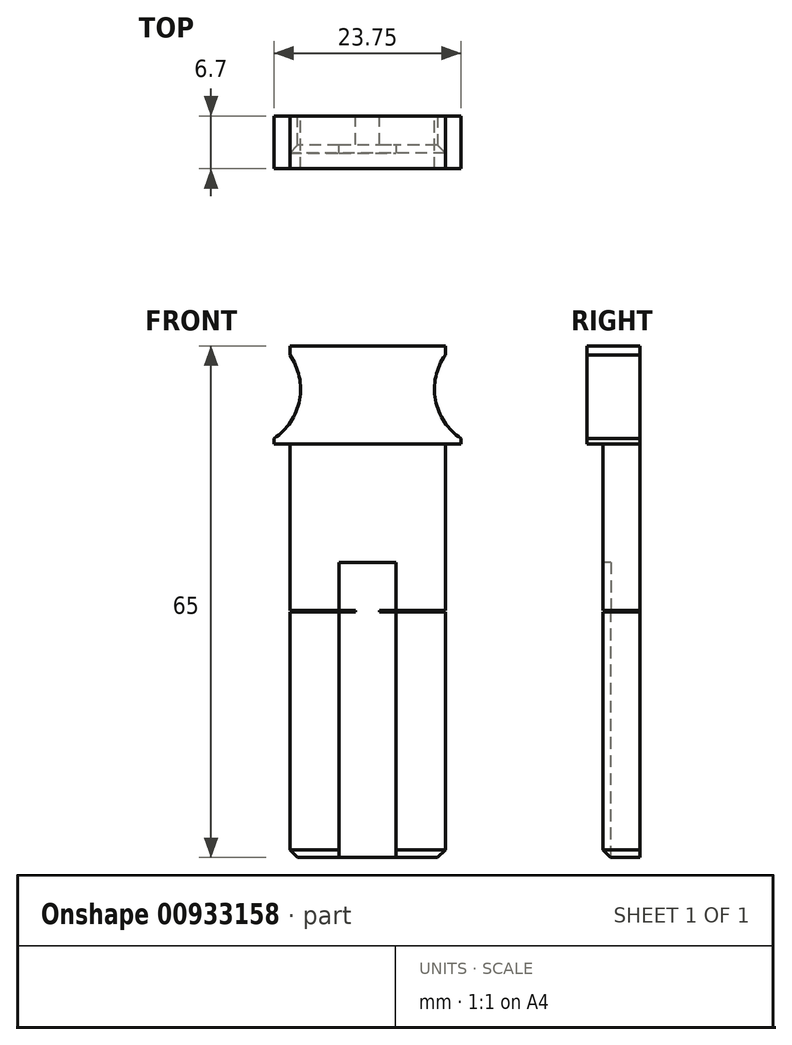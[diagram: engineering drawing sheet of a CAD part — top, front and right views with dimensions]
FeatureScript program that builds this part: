
annotation { "Feature Type Name" : "Feature", "Feature Type Description" : "" }
export const myFeature = defineFeature(function(context is Context, id is Id, definition is map)
    precondition{}
    {
        {
            var Q0;
            Q0=qCreatedBy(makeId("Front.planeOp"),FACE);
            var sketch = newSketch(context, id + "F0", { "sketchPlane" : qUnion([Q0])});
            skLineSegment(sketch, "E0.bottom", {"start": v(0, 0) * mm, "end": v(19.75, 0) * mm});
            skLineSegment(sketch, "E0.top", {"start": v(0, 65) * mm, "end": v(19.75, 65) * mm});
            skLineSegment(sketch, "E0.left", {"start": v(0, 0) * mm, "end": v(0, 65) * mm});
            skLineSegment(sketch, "E0.right", {"start": v(19.75, 0) * mm, "end": v(19.75, 65) * mm});
            skLineSegment(sketch, "E1", {"start": v(9.87, 65) * mm, "end": v(9.87, 0) * mm, "construction": true});
            skPoint(sketch, "E2", {"position": v(9.87, 38.5) * mm});
            skLineSegment(sketch, "E3", {"start": v(-8.82, 31.3) * mm, "end": v(33.74, 31.3) * mm, "construction": true});
            skLineSegment(sketch, "E4", {"start": v(0, 31.2) * mm, "end": v(0, 31.4) * mm});
            skCircle(sketch, "E5", {"center": v(25.88, 59.5) * mm, "radius": 7.5 * mm});
            skCircle(sketch, "E6.MirrorC", {"center": v(-6.13, 59.5) * mm, "radius": 7.5 * mm});
            skLineSegment(sketch, "E7.bottom", {"start": v(0, 31.4) * mm, "end": v(8.32, 31.4) * mm});
            skLineSegment(sketch, "E7.top", {"start": v(0, 31.4) * mm, "end": v(8.32, 31.4) * mm});
            skLineSegment(sketch, "E7.left", {"start": v(0, 31.4) * mm, "end": v(0, 31.4) * mm});
            skLineSegment(sketch, "E7.right", {"start": v(8.32, 31.4) * mm, "end": v(8.32, 31.4) * mm});
            skLineSegment(sketch, "E8", {"start": v(8.32, 31.4) * mm, "end": v(8.32, 31.2) * mm});
            skLineSegment(sketch, "E9", {"start": v(8.32, 31.2) * mm, "end": v(0, 31.2) * mm});
            skLineSegment(sketch, "E10", {"start": v(0, 31.4) * mm, "end": v(0, 31.2) * mm});
            skLineSegment(sketch, "E11.MirrorCS", {"start": v(19.75, 31.4) * mm, "end": v(11.43, 31.4) * mm});
            skLineSegment(sketch, "E12.MirrorCS", {"start": v(11.42, 31.4) * mm, "end": v(11.42, 31.2) * mm});
            skLineSegment(sketch, "E13.MirrorCS", {"start": v(11.43, 31.2) * mm, "end": v(19.75, 31.2) * mm});
            skLineSegment(sketch, "E14.MirrorCS", {"start": v(19.75, 31.4) * mm, "end": v(19.75, 31.2) * mm});
            skLineSegment(sketch, "E15.bottom", {"start": v(0, 52.5) * mm, "end": v(-2, 52.5) * mm});
            skLineSegment(sketch, "E15.top", {"start": v(0, 65.03) * mm, "end": v(-2, 65.03) * mm});
            skLineSegment(sketch, "E15.left", {"start": v(0, 52.5) * mm, "end": v(0, 65.03) * mm});
            skLineSegment(sketch, "E15.right", {"start": v(-2, 52.5) * mm, "end": v(-2, 65.03) * mm});
            skLineSegment(sketch, "E16.MirrorCS", {"start": v(19.75, 65.03) * mm, "end": v(21.75, 65.03) * mm});
            skLineSegment(sketch, "E17.MirrorCS", {"start": v(21.75, 52.5) * mm, "end": v(21.75, 65.03) * mm});
            skLineSegment(sketch, "E18.MirrorCS", {"start": v(19.75, 52.5) * mm, "end": v(21.75, 52.5) * mm});
            skSolve(sketch);
        }
        {
            var Q0;
            {var subQ3=sQuery(id+"F0.wireOp",EDGE,"E0.bottom");Q0=makeQuery(id+"F0.imprint","IMPRINT",FACE,{"disambiguationData":[TD([[makeQuery(id+"F0.imprint","IMPRINT",EDGE,{"derivedFrom":subQ3}),1.0]])]});}
            var Q1;
            {var subQ0=sQuery(id+"F0.wireOp",EDGE,"E15.bottom");Q1=makeQuery(id+"F0.imprint","IMPRINT",FACE,{"disambiguationData":[TD([[makeQuery(id+"F0.imprint","IMPRINT",EDGE,{"derivedFrom":subQ0}),-1.0]])]});}
            var Q2;
            {var subQ0=sQuery(id+"F0.wireOp",EDGE,"E18.MirrorCS");Q2=makeQuery(id+"F0.imprint","IMPRINT",FACE,{"disambiguationData":[TD([[makeQuery(id+"F0.imprint","IMPRINT",EDGE,{"derivedFrom":subQ0}),1.0]])]});}
            extrude(context, id + "F1", {"entities" : qUnion([Q0, Q1, Q2]), "depth" : 4.7 * mm, "offsetDistance" : 25 * mm});
        }
        {
            var Q0;
            Q0=makeQuery(id+"F1.opExtrude","CAP_FACE",FACE,{"disambiguationData":[OSD([sQuery(id+"F0.wireOp",EDGE,"E0.bottom"),sQuery(id+"F0.wireOp",EDGE,"E0.top"),sQuery(id+"F0.wireOp",EDGE,"E0.left"),sQuery(id+"F0.wireOp",EDGE,"E0.right"),sQuery(id+"F0.wireOp",EDGE,"E5"),sQuery(id+"F0.wireOp",EDGE,"E6.MirrorC"),sQuery(id+"F0.wireOp",EDGE,"E7.bottom"),sQuery(id+"F0.wireOp",EDGE,"E8"),sQuery(id+"F0.wireOp",EDGE,"E9"),sQuery(id+"F0.wireOp",EDGE,"E11.MirrorCS"),sQuery(id+"F0.wireOp",EDGE,"E12.MirrorCS"),sQuery(id+"F0.wireOp",EDGE,"E13.MirrorCS"),sQuery(id+"F0.wireOp",EDGE,"E15.bottom"),sQuery(id+"F0.wireOp",EDGE,"E15.right"),sQuery(id+"F0.wireOp",EDGE,"E17.MirrorCS"),sQuery(id+"F0.wireOp",EDGE,"E18.MirrorCS")])],"isStart":false});
            var sketch = newSketch(context, id + "F2", { "sketchPlane" : qUnion([Q0])});
            skLineSegment(sketch, "E19", {"start": v(6.27, 37.5) * mm, "end": v(13.47, 37.5) * mm});
            skLineSegment(sketch, "E20", {"start": v(13.47, 37.5) * mm, "end": v(13.47, 2.2) * mm});
            skLineSegment(sketch, "E21", {"start": v(13.47, 2.2) * mm, "end": v(13.47, 2.2) * mm});
            skLineSegment(sketch, "E22", {"start": v(13.47, 2.2) * mm, "end": v(13.47, 0) * mm});
            skLineSegment(sketch, "E23", {"start": v(13.47, 0) * mm, "end": v(6.27, 0) * mm});
            skLineSegment(sketch, "E24", {"start": v(6.27, 0) * mm, "end": v(6.27, 2.2) * mm});
            skLineSegment(sketch, "E25", {"start": v(6.27, 2.2) * mm, "end": v(6.27, 2.2) * mm});
            skLineSegment(sketch, "E26", {"start": v(6.27, 2.2) * mm, "end": v(6.27, 37.5) * mm});
            skLineSegment(sketch, "E27", {"start": v(9.87, 65) * mm, "end": v(9.87, 0) * mm, "construction": true});
            skSolve(sketch);
        }
        {
            var Q0;
            Q0=qSketchRegion(id+"F2",true);
            extrude(context, id + "F3", {"entities" : qUnion([Q0]), "operationType" : NewBodyOperationType.REMOVE, "oppositeDirection" : true, "depth" : 1.05 * mm, "offsetDistance" : 25 * mm});
        }
        {
            var Q0;
            {var subQ0=sQuery(id+"F0.wireOp",EDGE,"E0.right");Q0=qUnion([makeQuery(id+"F1.opExtrude","SWEPT_FACE",FACE,{"disambiguationData":[OSD([subQ0]),TDD([makeQuery(id+"F0.imprint","IMPRINT",EDGE,{"disambiguationData":[TD([[makeQuery(id+"F0.imprint","INTERSECT",VERTEX,{"derivedFrom":[sQuery(id+"F0.wireOp",EDGE,"E0.bottom"),subQ0]}),-1.0]])],"derivedFrom":subQ0})])]}),makeQuery(id+"F1.opExtrude","SWEPT_FACE",FACE,{"disambiguationData":[OSD([subQ0]),TDD([makeQuery(id+"F0.imprint","IMPRINT",EDGE,{"disambiguationData":[TD([[makeQuery(id+"F0.imprint","INTERSECT",VERTEX,{"derivedFrom":[subQ0,sQuery(id+"F0.wireOp",EDGE,"E11.MirrorCS")]}),-1.0]])],"derivedFrom":subQ0})])]}),makeQuery(id+"F1.opExtrude","SWEPT_FACE",FACE,{"disambiguationData":[OSD([subQ0]),TDD([makeQuery(id+"F0.imprint","IMPRINT",EDGE,{"disambiguationData":[TD([[makeQuery(id+"F0.imprint","INTERSECT",VERTEX,{"derivedFrom":[sQuery(id+"F0.wireOp",EDGE,"E0.top"),subQ0]}),1.0]])],"derivedFrom":subQ0})])]})]);}
            var sketch = newSketch(context, id + "F4", { "sketchPlane" : qUnion([Q0])});
            skLineSegment(sketch, "E28", {"start": v(-15.64, 31.3) * mm, "end": v(17.74, 31.3) * mm, "construction": true});
            skLineSegment(sketch, "E29", {"start": v(-1, 31.3) * mm, "end": v(0, 32.3) * mm});
            skLineSegment(sketch, "E30", {"start": v(0, 32.3) * mm, "end": v(0, 30.3) * mm});
            skLineSegment(sketch, "E31", {"start": v(0, 30.3) * mm, "end": v(-1, 31.3) * mm});
            skSolve(sketch);
        }
        {
            var Q0;
            {var subQ0=sQuery(id+"F0.wireOp",EDGE,"E15.bottom");var subQ1=sQuery(id+"F0.wireOp",EDGE,"E11.MirrorCS");var subQ2=sQuery(id+"F0.wireOp",EDGE,"E7.bottom");var subQ3=sQuery(id+"F0.wireOp",EDGE,"E6.MirrorC");var subQ4=sQuery(id+"F0.wireOp",EDGE,"E5");var subQ5=sQuery(id+"F0.wireOp",EDGE,"E0.right");var subQ6=sQuery(id+"F0.wireOp",EDGE,"E0.top");var subQ7=sQuery(id+"F0.wireOp",EDGE,"E18.MirrorCS");var subQ8=sQuery(id+"F0.wireOp",EDGE,"E0.left");var subQ9=sQuery(id+"F0.wireOp",EDGE,"E15.right");var subQ10=sQuery(id+"F0.wireOp",EDGE,"E17.MirrorCS");Q0=makeQuery(id+"F3.boolean.opBoolean","SPLIT",FACE,{"disambiguationData":[TD([makeQuery(id+"F1.opExtrude","SWEPT_FACE",FACE,{"disambiguationData":[OSD([subQ6])]})])],"derivedFrom":makeQuery(id+"F1.opExtrude","CAP_FACE",FACE,{"disambiguationData":[OSD([sQuery(id+"F0.wireOp",EDGE,"E0.bottom"),subQ6,subQ8,subQ5,subQ4,subQ3,subQ2,sQuery(id+"F0.wireOp",EDGE,"E8"),sQuery(id+"F0.wireOp",EDGE,"E9"),subQ1,sQuery(id+"F0.wireOp",EDGE,"E12.MirrorCS"),sQuery(id+"F0.wireOp",EDGE,"E13.MirrorCS"),subQ0,subQ9,subQ10,subQ7])],"isStart":false})});}
            var sketch = newSketch(context, id + "F5", { "sketchPlane" : qUnion([Q0])});
            skLineSegment(sketch, "E32", {"start": v(0, 52.5) * mm, "end": v(19.75, 52.5) * mm});
            skSolve(sketch);
        }
        {
            var Q0;
            Q0=makeQuery(id+"F5.imprint","IMPRINT",FACE,{"disambiguationData":[TD([[makeQuery(id+"F5.imprint","IMPRINT",EDGE,{"derivedFrom":sQuery(id+"F5.wireOp",EDGE,"E32")}),1.0]])]});
            extrude(context, id + "F6", {"entities" : qUnion([Q0]), "operationType" : NewBodyOperationType.ADD, "depth" : 2 * mm, "offsetDistance" : 25 * mm});
        }
        {
            var Q0;
            Q0=makeQuery(id+"F1.opExtrude","SWEPT_EDGE",EDGE,{"disambiguationData":[OSD([sQuery(id+"F0.wireOp",EDGE,"E0.bottom"),sQuery(id+"F0.wireOp",EDGE,"E0.left")])]});
            var Q1;
            Q1=makeQuery(id+"F1.opExtrude","SWEPT_EDGE",EDGE,{"disambiguationData":[OSD([sQuery(id+"F0.wireOp",EDGE,"E0.bottom"),sQuery(id+"F0.wireOp",EDGE,"E0.right")])]});
            var Q2;
            {var subQ0=sQuery(id+"F0.wireOp",EDGE,"E0.bottom");Q2=makeQuery(id+"F3.boolean.opBoolean","SPLIT",EDGE,{"disambiguationData":[TD([makeQuery(id+"F3.opExtrude","SWEPT_FACE",FACE,{"disambiguationData":[OSD([sQuery(id+"F2.wireOp",EDGE,"E24"),sQuery(id+"F2.wireOp",EDGE,"E26")])]})])],"derivedFrom":makeQuery(id+"F1.opExtrude","CAP_EDGE",EDGE,{"disambiguationData":[OSD([subQ0])],"isStart":false})});}
            var Q3;
            {var subQ0=sQuery(id+"F0.wireOp",EDGE,"E0.bottom");Q3=makeQuery(id+"F3.boolean.opBoolean","SPLIT",EDGE,{"disambiguationData":[TD([makeQuery(id+"F3.opExtrude","SWEPT_FACE",FACE,{"disambiguationData":[OSD([sQuery(id+"F2.wireOp",EDGE,"E20"),sQuery(id+"F2.wireOp",EDGE,"E22")])]})])],"derivedFrom":makeQuery(id+"F1.opExtrude","CAP_EDGE",EDGE,{"disambiguationData":[OSD([subQ0])],"isStart":false})});}
            var Q4;
            Q4=makeQuery(id+"F3.boolean.opBoolean","COPY",EDGE,{"derivedFrom":makeQuery(id+"F3.opExtrude","CAP_EDGE",EDGE,{"disambiguationData":[OSD([sQuery(id+"F2.wireOp",EDGE,"E23")])],"isStart":false})});
            chamfer(context, id + "F7", {"entities" : qUnion([Q0, Q1, Q2, Q3, Q4]), "width" : 1 * mm, "tangentPropagation" : true});
        }
    });
